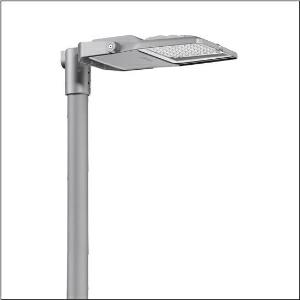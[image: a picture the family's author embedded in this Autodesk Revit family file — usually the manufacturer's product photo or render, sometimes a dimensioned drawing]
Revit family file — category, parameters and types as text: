
# Revit family: floodlight_fl_21_iq_mini___pl43_5xa7771c2a3a_69d2
name_source: partatom
category: Lighting Fixtures
units: mm (PartAtom-declared; Revit-internal decimal feet)

## family parameters
Cut with Voids When Loaded = No
Host = Face
Light Source = No
Part Type = Normal
Room Calculation Point = No
Round Connector Dimension = Use Diameter
Shared = No

## types (1)
- --- (1 x LED, 12520 lm, 87.2 W, 3000K)
    Apparent Load = 87 VA
    CIE Flux Codes = 27 78 99 100 100
    Color Rendering = 70
    Color Temperature = 3000K
    Default Elevation = 1800 mm
    Description = Floodlight FL 21 iQ mini, floodlight, primary light control with lens, of PMMA, primary optical cover: protective disc, of toughened safety glass, transparent, light distribution: PL43, light emission: direct distribution, installation type: surface-mounted, LED, High Power LED, rated luminous flux: 12.520lm, luminous efficacy: 144lm/W, light colour: 730, colour temperature: 3000K, control: Auto-Match, Temp-Guard, Lumen-Switch, Night-Set, Smart-Wire, Light-Fading, Desk-Remote (wireless, voltage-free reading and setting of iQ features in the workshop via application-optimized NFC function/RFID function), optimised constant luminous flux control (CLO 2.0), with terminal, 6-pole, mains connection: 220..240V, AC, 50/60Hz, start of lifetime: 87W, end of service life: 92W, reduction: 40W, luminaire housing, of diecast aluminium, powder-coated, Siteco® metallic grey (DB 702S), corrosivity category C5 mid according to DIN EN ISO 12944, sealing non-destructively replaceable, please order mast flange separately, mast bracket, of steel, galvanised, powder-coated, Siteco® metallic grey (DB 702S), protection rating (complete): IP66, insulation class (complete): insulation class II (safety insulation), certification: CE, ENEC, VDE, protection symbol: D, impact resistance: IK08, permissible operating ambient temperature: -40..+40°C, permissible operating ambient temperature for outdoor applications: -40..+50°C, standard: DIN EN 12944, LABS conformity tested according to VDMA 24364:2018-05, packaging unit: 1 piece

Light Distribution: PL43
    Height = 70 mm
    Lamp = 1 x LED
    Lamp Light Flux = 12520 lm
    Lamp Power = 87.2 W
    Lamp count = 1
    Length = 485 mm
    Luminous efficacy = 144 lm/W
    Manufacturer = Siteco
    ModVariant = No
    Model = 5XA7771C2A3A
    Number of Poles = 1
    OnlyDefault = Yes
    Power Factor = 1
    Product Name = Floodlight FL 21 iQ mini | PL43
    Product group = floodlight | pylon annexe
    ProductGroupID = 6200
    Protection Class = Protection class II
    Protection Degree = IP 66
    RLX_Detail_Level = 1
    RLX_Emergency_Light_Flux = 0 lm
    RLX_Emergency_Type = 0
    RLX_Emergency_Type_DB = No
    RlxData = <blob elided: 101217 chars, md5=bc30977a>
    Socket = socket
    Standby Power = 0 W
    System Light Flux = 12520 lm
    System Power = 87 W
    Type Comments = factory setting: luminous flux: 100 % | dim-lin: 254 | 456 mA
    Type Image = l_1007125.jpg
    URL = http://relux.com
    VarID = @adj_132835
    Voltage = 0 V
    Weight = 0.00 kg
    Width = 337 mm

## geometry (parser evidence)
native form markers: Blend x4, Sweep x14
no freeform markers — native parametric forms only
